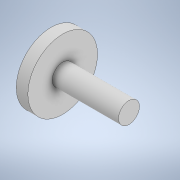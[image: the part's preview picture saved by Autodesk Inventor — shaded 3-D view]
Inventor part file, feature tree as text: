
AUTODESK INVENTOR PART (.ipt)
format: ipt  version: 2020 (Build 240168000, 168)  size: 102,912 bytes
history: native  units: mm
features: revolve x1, sketch x1
ambient origin geometry x8: Origin, YZ Plane, XZ Plane, XY Plane, X Axis, Y Axis, Z Axis, Center Point
bodies: Solid1 (feature_tree)
feature tree (2):
  revolve  "Revolution1"  [1 undecoded]
  sketch  "Sketch1"  dims[d0=3.0mm d1=10.0mm d3=9.0mm d4=90.0deg]
note: 1 required parameter value undecoded (feature->parameter linkage not recoverable at this tier; creation-order binding heuristic only, values carry confidence <= 0.55)
